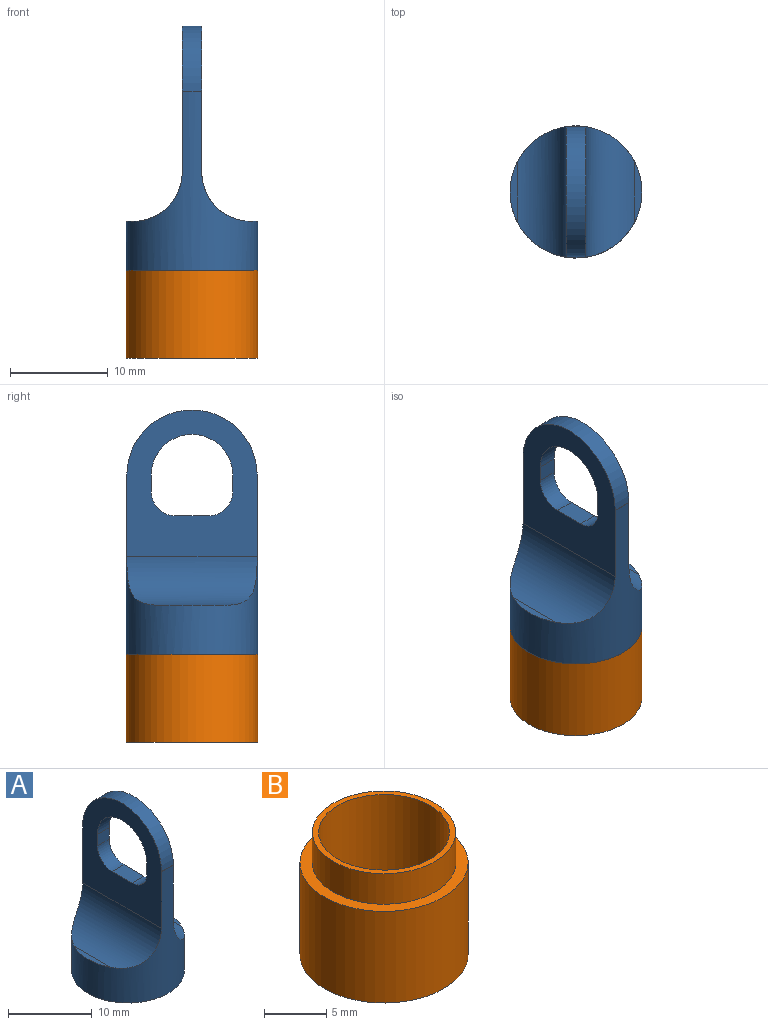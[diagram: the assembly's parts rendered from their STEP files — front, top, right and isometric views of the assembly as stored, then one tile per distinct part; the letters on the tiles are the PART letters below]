
ASSEMBLY  parts=2 mates=1
PART A: 19 faces, bbox 13.5x13.5x25 mm
  f0: cylinder r=6.75mm len=18.32mm, axis (0,0,-1), area 288.6mm2, adj f1,f2,f3,f5,f6,f13,f14,f17
  f1: plane 15x13.35mm, normal (1,0,0), area 121.6mm2, adj f0,f8,f9,f10,f11,f12,f15,f16
  f2: plane 15x13.35mm, normal (-1,0,0), area 121.6mm2, adj f0,f8,f9,f10,f11,f12,f15,f16
  f3: plane 6.18x0.75mm, normal (0,0,1), area 3.1mm2, adj f0,f17
  f4: cylinder r=5.75mm len=11.5mm, axis (0,0,-1), area 108.4mm2, adj f6,f7
  f5: plane 6.18x0.75mm, normal (0,0,1), area 3.1mm2, adj f0,f18
  f6: plane 13.5x13.5mm, normal (0,0,-1), area 39.3mm2, adj f0,f4
  f7: plane 11.5x11.5mm, normal (0,0,-1), area 103.9mm2, adj f4
  f8: cylinder r=6.68mm len=13.35mm, axis (1,0,0), area 41.9mm2, adj f1,f2,f13,f14
  f9: cylinder r=4.18mm len=8.35mm, axis (1,0,0), area 26.2mm2, adj f1,f2,f10,f12
  f10: plane 2x1.68mm, normal (0,1,0), area 3.4mm2, adj f1,f2,f9,f15
  f11: plane 3.35x2mm, normal (0,0,1), area 6.7mm2, adj f1,f2,f15,f16
  f12: plane 2x1.68mm, normal (0,-1,0), area 3.4mm2, adj f1,f2,f9,f16
  f13: plane 2x0.07mm, normal (0,0,1), area 0.1mm2, adj f0,f8
  f14: plane 2x0.07mm, normal (0,0,1), area 0.1mm2, adj f0,f8
  f15: cylinder r=2.5mm len=2.5mm, axis (-1,0,0), area 7.9mm2, adj f1,f2,f10,f11
  f16: cylinder r=2.5mm len=2.5mm, axis (1,0,0), area 7.9mm2, adj f1,f2,f11,f12
  f17: cylinder r=5mm len=13.35mm, axis (0,1,0), area 92.1mm2, adj f0,f1,f3
  f18: cylinder r=5mm len=13.35mm, axis (0,-1,0), area 92.1mm2, adj f0,f2,f5
PART B: 8 faces, bbox 13.5x13.5x12 mm
  f0: cylinder r=6.75mm len=13.5mm, axis (0,0,-1), area 381.7mm2, adj f5,f7
  f1: plane 11.5x11.5mm, normal (0,0,1), area 17.3mm2, adj f2,f6
  f2: cylinder r=5.25mm len=11mm, axis (0,0,-1), area 362.9mm2, adj f1,f3
  f3: plane 10.5x10.5mm, normal (0,0,1), area 42.4mm2, adj f2,f4
  f4: cylinder r=3.75mm len=7.5mm, axis (0,0,1), area 23.6mm2, adj f3,f5
  f5: plane 13.5x13.5mm, normal (0,0,-1), area 99mm2, adj f0,f4
  f6: cylinder r=5.75mm len=11.5mm, axis (0,0,1), area 108.4mm2, adj f1,f7
  f7: plane 13.5x13.5mm, normal (0,0,1), area 39.3mm2, adj f0,f6
PLACE A t=(-5.05,-0.15,7.14)mm
PLACE B t=(-5.05,-0.15,-0.86)mm
MATE fastened A.f4 <-> B.f2  axis (0,0,-1) through (-5.05,-0.15,10.14)mm
